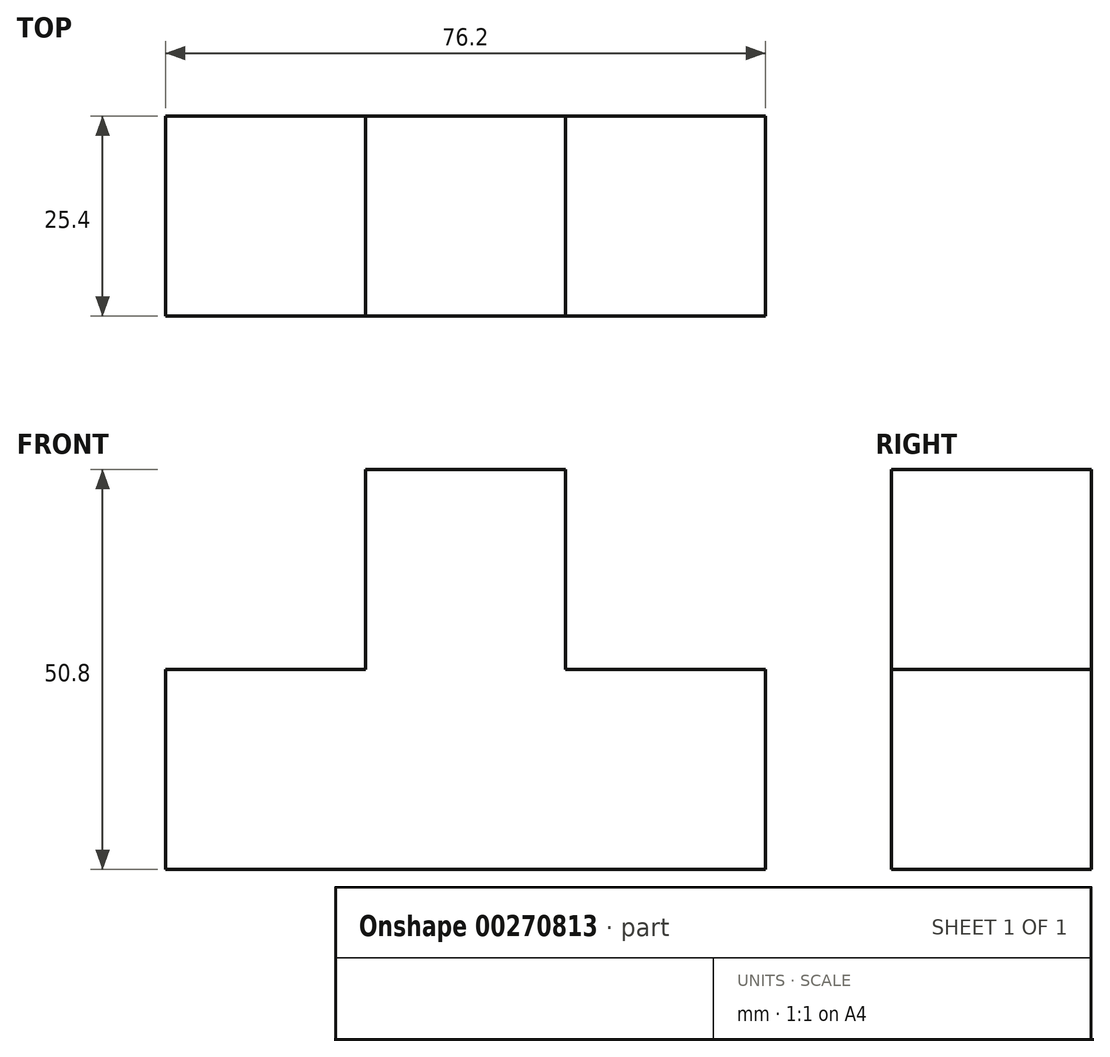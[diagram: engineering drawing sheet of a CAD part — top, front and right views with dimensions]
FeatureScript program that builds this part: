
annotation { "Feature Type Name" : "Feature", "Feature Type Description" : "" }
export const myFeature = defineFeature(function(context is Context, id is Id, definition is map)
    precondition{}
    {
        {
            var Q0;
            Q0=qCreatedBy(makeId("Front.planeOp"),FACE);
            var sketch = newSketch(context, id + "F0", { "sketchPlane" : qUnion([Q0])});
            skPoint(sketch, "E0.end.orphan", {"position": v(-76.2, 25.4) * mm});
            skPoint(sketch, "E1.end.orphan", {"position": v(-38.1, 25.4) * mm});
            skPoint(sketch, "E2.start.orphan", {"position": v(0, 25.4) * mm});
            skLineSegment(sketch, "E3", {"start": v(0, 0) * mm, "end": v(-76.2, 0) * mm});
            skLineSegment(sketch, "E4", {"start": v(-76.2, 0) * mm, "end": v(-76.2, 25.4) * mm});
            skLineSegment(sketch, "E5", {"start": v(-50.8, 25.4) * mm, "end": v(-76.2, 25.4) * mm});
            skLineSegment(sketch, "E6", {"start": v(-50.8, 25.4) * mm, "end": v(-50.8, 50.8) * mm});
            skLineSegment(sketch, "E7", {"start": v(-50.8, 50.8) * mm, "end": v(-25.4, 50.8) * mm});
            skLineSegment(sketch, "E8", {"start": v(-25.4, 50.8) * mm, "end": v(-25.4, 25.4) * mm});
            skLineSegment(sketch, "E9", {"start": v(-25.4, 25.4) * mm, "end": v(0, 25.4) * mm});
            skLineSegment(sketch, "E10", {"start": v(0, 0) * mm, "end": v(0, 25.4) * mm});
            skSolve(sketch);
        }
        {
            var Q0;
            Q0=makeQuery(id+"F0.imprint","IMPRINT",FACE,{"disambiguationData":[TD([[makeQuery(id+"F0.imprint","IMPRINT",EDGE,{"derivedFrom":sQuery(id+"F0.wireOp",EDGE,"E3")}),-1.0]])]});
            extrude(context, id + "F1", {"entities" : qUnion([Q0]), "depth" : 25.4 * mm});
        }
    });
